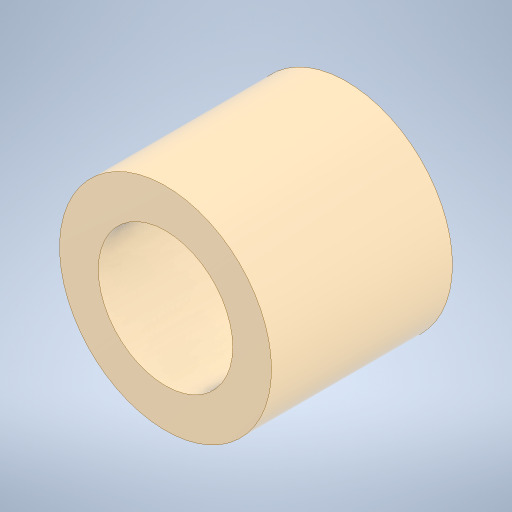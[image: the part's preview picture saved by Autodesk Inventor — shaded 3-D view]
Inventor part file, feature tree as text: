
AUTODESK INVENTOR PART (.ipt)
format: ipt  version: 2024 (Build 280153000, 153)  size: 208,896 bytes
history: native  units: in
note: dims shown in document units (in); Inventor stores cm internally (conversion verified against a paired STEP export)
features: extrude x2, sketch x1
ambient origin geometry x8: Origin, YZ Plane, XZ Plane, XY Plane, X Axis, Y Axis, Z Axis, Center Point
bodies: Solid1 (feature_tree)
feature tree (3):
  sketch  "Sketch1"  dims[d0=0.2047in d1=0.3228in d2=0.0197in d3=0.0in d4=0.2756in d5=0.0in]
  extrude  "Extrusion1"  Depth=0.2756in
  extrude  "Extrusion2"  Depth=0.0197in TaperAngle=0.0deg
